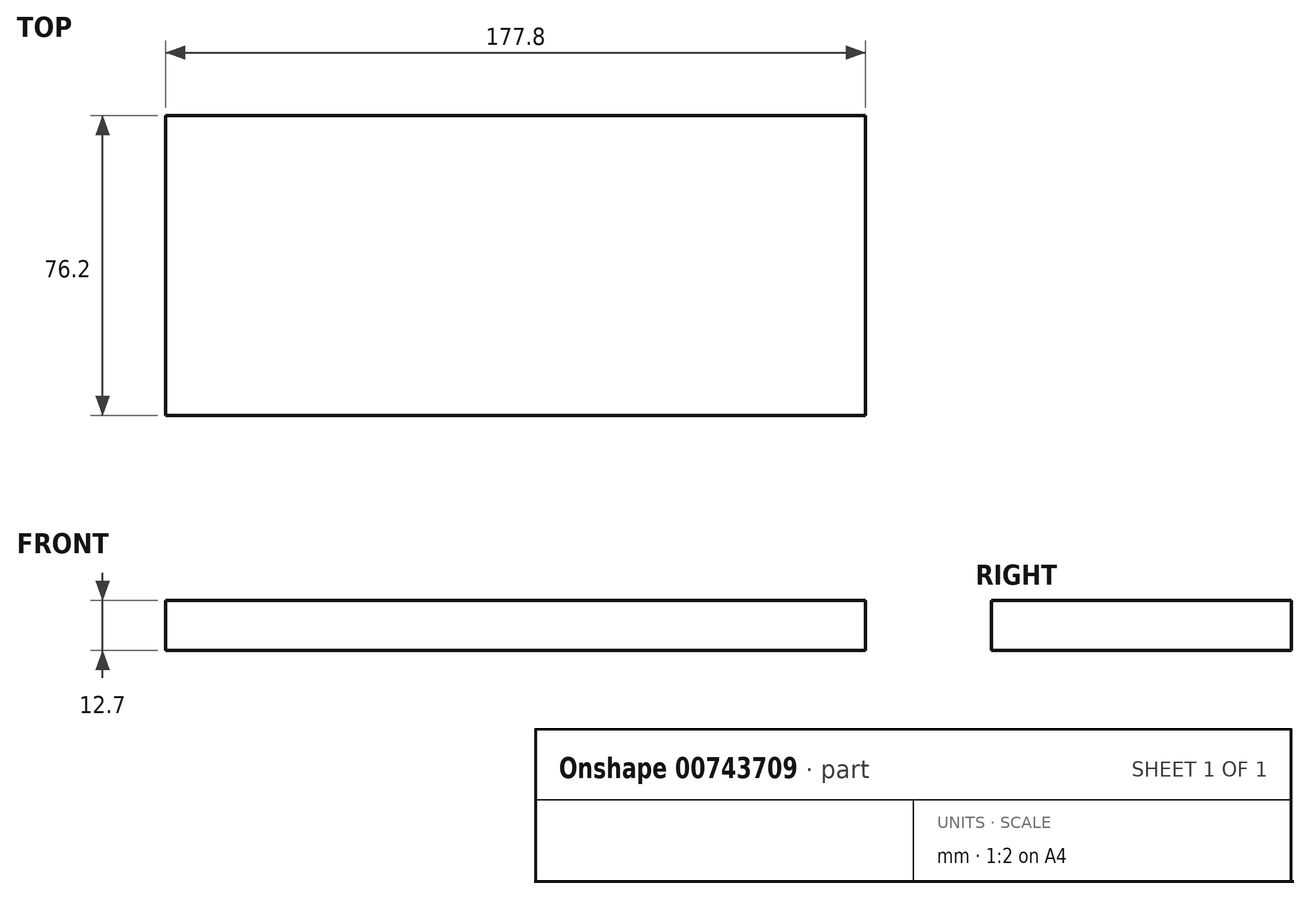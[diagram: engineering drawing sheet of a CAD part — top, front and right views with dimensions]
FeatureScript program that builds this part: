
annotation { "Feature Type Name" : "Feature", "Feature Type Description" : "" }
export const myFeature = defineFeature(function(context is Context, id is Id, definition is map)
    precondition{}
    {
        {
            var Q0;
            Q0=qCreatedBy(makeId("Top.planeOp"),FACE);
            var sketch = newSketch(context, id + "F0", { "sketchPlane" : qUnion([Q0])});
            skLineSegment(sketch, "E0.bottom", {"start": v(-130.37, 65.84) * mm, "end": v(47.43, 65.84) * mm});
            skLineSegment(sketch, "E0.top", {"start": v(-130.37, -10.36) * mm, "end": v(47.43, -10.36) * mm});
            skLineSegment(sketch, "E0.left", {"start": v(-130.37, 65.84) * mm, "end": v(-130.37, -10.36) * mm});
            skLineSegment(sketch, "E0.right", {"start": v(47.43, 65.84) * mm, "end": v(47.43, -10.36) * mm});
            skSolve(sketch);
        }
        {
            var Q0;
            Q0=makeQuery(id+"F0.imprint","IMPRINT",FACE,{"disambiguationData":[TD([[makeQuery(id+"F0.imprint","IMPRINT",EDGE,{"derivedFrom":sQuery(id+"F0.wireOp",EDGE,"E0.bottom")}),-1.0]])]});
            extrude(context, id + "F1", {"entities" : qUnion([Q0]), "depth" : 12.7 * mm, "offsetDistance" : 25.4 * mm});
        }
    });
